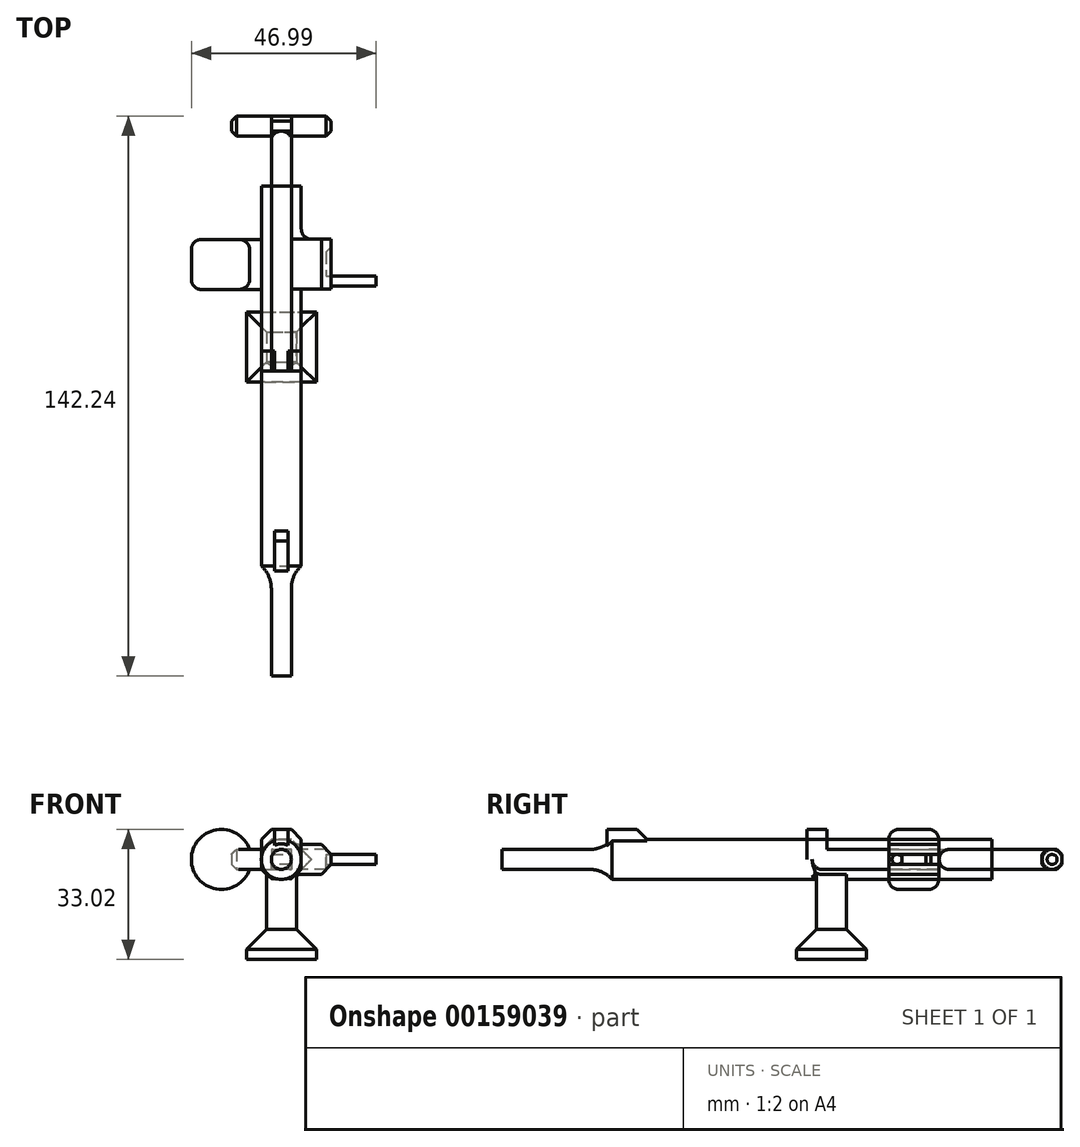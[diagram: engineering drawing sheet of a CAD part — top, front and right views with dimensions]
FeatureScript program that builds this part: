
annotation { "Feature Type Name" : "Feature", "Feature Type Description" : "" }
export const myFeature = defineFeature(function(context is Context, id is Id, definition is map)
    precondition{}
    {
        {
            var Q0;
            Q0=qCreatedBy(makeId("Top.planeOp"),FACE);
            var sketch = newSketch(context, id + "F0", { "sketchPlane" : qUnion([Q0])});
            skLineSegment(sketch, "E0.bottom", {"start": v(5.08, 6.35) * mm, "end": v(-5.08, 6.35) * mm});
            skLineSegment(sketch, "E0.top", {"start": v(5.08, -6.35) * mm, "end": v(-5.08, -6.35) * mm});
            skLineSegment(sketch, "E0.left", {"start": v(5.08, 6.35) * mm, "end": v(5.08, -6.35) * mm});
            skLineSegment(sketch, "E0.right", {"start": v(-5.08, 6.35) * mm, "end": v(-5.08, -6.35) * mm});
            skPoint(sketch, "E0.middle", {"position": v(0, 0) * mm});
            skSolve(sketch);
        }
        {
            var Q0;
            Q0=makeQuery(id+"F0.imprint","IMPRINT",FACE,{"disambiguationData":[TD([[makeQuery(id+"F0.imprint","IMPRINT",EDGE,{"derivedFrom":sQuery(id+"F0.wireOp",EDGE,"E0.bottom")}),1.0]])]});
            extrude(context, id + "F1", {"entities" : qUnion([Q0]), "endBound" : BoundingType.SYMMETRIC, "depth" : 10.16 * mm});
        }
        {
            var Q0;
            Q0=makeQuery(id+"F1.opExtrude","SWEPT_FACE",FACE,{"disambiguationData":[OSD([sQuery(id+"F0.wireOp",EDGE,"E0.top")])]});
            var sketch = newSketch(context, id + "F2", { "sketchPlane" : qUnion([Q0])});
            skCircle(sketch, "E1", {"center": v(0, 0) * mm, "radius": 5.08 * mm});
            skSolve(sketch);
        }
        {
            var Q0;
            {var subQ0=sQuery(id+"F2.wireOp",EDGE,"E1");var subQ1=sQuery(id+"F0.wireOp",EDGE,"E0.top");var subQ2=makeQuery(id+"F2.imprint","INTERSECT",VERTEX,{"derivedFrom":[makeQuery(id+"F1.opExtrude","CAP_EDGE",EDGE,{"disambiguationData":[OSD([subQ1])],"isStart":false}),subQ0]});Q0=makeQuery(id+"F2.imprint","IMPRINT",FACE,{"disambiguationData":[TD([[makeQuery(id+"F2.imprint","IMPRINT",EDGE,{"disambiguationData":[TD([[subQ2,1.0]])],"derivedFrom":subQ0}),1.0]])]});}
            extrude(context, id + "F3", {"entities" : qUnion([Q0]), "operationType" : NewBodyOperationType.ADD, "depth" : 50.8 * mm});
        }
        {
            var Q0;
            Q0=makeQuery(id+"F1.opExtrude","SWEPT_FACE",FACE,{"disambiguationData":[OSD([sQuery(id+"F0.wireOp",EDGE,"E0.bottom")])]});
            extrude(context, id + "F4", {"entities" : qUnion([Q0]), "operationType" : NewBodyOperationType.ADD, "depth" : 25.4 * mm});
        }
        {
            var Q0;
            {var subQ0=sQuery(id+"F0.wireOp",EDGE,"E0.left");var subQ1=sQuery(id+"F0.wireOp",EDGE,"E0.top");Q0=makeQuery(id+"F3.boolean.opBoolean","SPLIT",EDGE,{"disambiguationData":[TD([makeQuery(id+"F1.opExtrude","SWEPT_FACE",FACE,{"disambiguationData":[OSD([subQ0])]})])],"derivedFrom":makeQuery(id+"F1.opExtrude","CAP_EDGE",EDGE,{"disambiguationData":[OSD([subQ1])],"isStart":false})});}
            var Q1;
            {var subQ0=sQuery(id+"F0.wireOp",EDGE,"E0.right");var subQ1=sQuery(id+"F0.wireOp",EDGE,"E0.top");Q1=makeQuery(id+"F3.boolean.opBoolean","SPLIT",EDGE,{"disambiguationData":[TD([makeQuery(id+"F1.opExtrude","SWEPT_FACE",FACE,{"disambiguationData":[OSD([subQ0])]})])],"derivedFrom":makeQuery(id+"F1.opExtrude","CAP_EDGE",EDGE,{"disambiguationData":[OSD([subQ1])],"isStart":true})});}
            fillet(context, id + "F5", {"entities" : qUnion([Q0, Q1]), "radius" : 5.08 * mm, "tangentPropagation" : true, "allowEdgeOverflow" : false});
        }
        {
            var Q0;
            {var subQ0=sQuery(id+"F0.wireOp",EDGE,"E0.right");var subQ1=sQuery(id+"F0.wireOp",EDGE,"E0.bottom");Q0=makeQuery(id+"F4.boolean.opBoolean","MERGE",EDGE,{"derivedFrom":[makeQuery(id+"F1.opExtrude","CAP_EDGE",EDGE,{"disambiguationData":[OSD([subQ0])],"isStart":false}),makeQuery(id+"F4.opExtrude","SWEPT_EDGE",EDGE,{"disambiguationData":[OSD([subQ1,subQ0]),TDD([makeQuery(id+"F1.opExtrude","CAP_VERTEX",VERTEX,{"disambiguationData":[OSD([subQ1,subQ0])],"isStart":false})])]})]});}
            var Q1;
            {var subQ0=sQuery(id+"F0.wireOp",EDGE,"E0.right");var subQ1=sQuery(id+"F0.wireOp",EDGE,"E0.bottom");Q1=makeQuery(id+"F4.boolean.opBoolean","MERGE",EDGE,{"derivedFrom":[makeQuery(id+"F1.opExtrude","CAP_EDGE",EDGE,{"disambiguationData":[OSD([subQ0])],"isStart":true}),makeQuery(id+"F4.opExtrude","SWEPT_EDGE",EDGE,{"disambiguationData":[OSD([subQ1,subQ0]),TDD([makeQuery(id+"F1.opExtrude","CAP_VERTEX",VERTEX,{"disambiguationData":[OSD([subQ1,subQ0])],"isStart":true})])]})]});}
            var Q2;
            {var subQ0=sQuery(id+"F0.wireOp",EDGE,"E0.left");var subQ1=sQuery(id+"F0.wireOp",EDGE,"E0.bottom");Q2=makeQuery(id+"F4.boolean.opBoolean","MERGE",EDGE,{"derivedFrom":[makeQuery(id+"F1.opExtrude","CAP_EDGE",EDGE,{"disambiguationData":[OSD([subQ0])],"isStart":false}),makeQuery(id+"F4.opExtrude","SWEPT_EDGE",EDGE,{"disambiguationData":[OSD([subQ1,subQ0]),TDD([makeQuery(id+"F1.opExtrude","CAP_VERTEX",VERTEX,{"disambiguationData":[OSD([subQ1,subQ0])],"isStart":false})])]})]});}
            var Q3;
            {var subQ0=sQuery(id+"F0.wireOp",EDGE,"E0.left");var subQ1=sQuery(id+"F0.wireOp",EDGE,"E0.bottom");Q3=makeQuery(id+"F4.boolean.opBoolean","MERGE",EDGE,{"derivedFrom":[makeQuery(id+"F1.opExtrude","CAP_EDGE",EDGE,{"disambiguationData":[OSD([subQ0])],"isStart":true}),makeQuery(id+"F4.opExtrude","SWEPT_EDGE",EDGE,{"disambiguationData":[OSD([subQ1,subQ0]),TDD([makeQuery(id+"F1.opExtrude","CAP_VERTEX",VERTEX,{"disambiguationData":[OSD([subQ1,subQ0])],"isStart":true})])]})]});}
            var Q4;
            Q4=makeQuery(id+"F3.opExtrude","CAP_EDGE",EDGE,{"disambiguationData":[OSD([sQuery(id+"F2.wireOp",EDGE,"E1")])],"isStart":false});
            chamfer(context, id + "F6", {"entities" : qUnion([Q0, Q1, Q2, Q3, Q4]), "width" : 2.54 * mm, "tangentPropagation" : true});
        }
        {
            var Q0;
            {var subQ0=sQuery(id+"F0.wireOp",EDGE,"E0.bottom");Q0=makeQuery(id+"F4.boolean.opBoolean","MERGE",FACE,{"derivedFrom":[makeQuery(id+"F1.opExtrude","CAP_FACE",FACE,{"disambiguationData":[OSD([subQ0,sQuery(id+"F0.wireOp",EDGE,"E0.top"),sQuery(id+"F0.wireOp",EDGE,"E0.left"),sQuery(id+"F0.wireOp",EDGE,"E0.right")])],"isStart":true}),makeQuery(id+"F4.opExtrude","SWEPT_FACE",FACE,{"disambiguationData":[OSD([subQ0]),TDD([makeQuery(id+"F1.opExtrude","CAP_EDGE",EDGE,{"disambiguationData":[OSD([subQ0])],"isStart":true})])]})]});}
            var sketch = newSketch(context, id + "F7", { "sketchPlane" : qUnion([Q0])});
            skPoint(sketch, "E2.middle", {"position": v(0, 0) * mm});
            skLineSegment(sketch, "E3.bottom", {"start": v(-3.8, -4.85) * mm, "end": v(3.81, -4.85) * mm});
            skLineSegment(sketch, "E3.top", {"start": v(-3.81, 2.77) * mm, "end": v(3.8, 2.77) * mm});
            skLineSegment(sketch, "E3.left", {"start": v(-3.8, -4.85) * mm, "end": v(-3.81, 2.77) * mm});
            skLineSegment(sketch, "E3.right", {"start": v(3.81, -4.85) * mm, "end": v(3.8, 2.77) * mm});
            skPoint(sketch, "E3.middle", {"position": v(0, -1.04) * mm});
            skSolve(sketch);
        }
        {
            var Q0;
            Q0 = qSketchRegion(id + "F7", true);
            extrude(context, id + "F8", {"entities" : qUnion([Q0]), "operationType" : NewBodyOperationType.ADD, "endBound" : BoundingType.SYMMETRIC, "depth" : 15.24 * mm});
        }
        {
            var Q0;
            Q0=makeQuery(id+"F8.opExtrude","CAP_FACE",FACE,{"disambiguationData":[OSD([sQuery(id+"F7.wireOp",EDGE,"E3.bottom"),sQuery(id+"F7.wireOp",EDGE,"E3.top"),sQuery(id+"F7.wireOp",EDGE,"E3.left"),sQuery(id+"F7.wireOp",EDGE,"E3.right")])],"isStart":false});
            extrude(context, id + "F9", {"entities" : qUnion([Q0]), "operationType" : NewBodyOperationType.ADD, "depth" : 5.08 * mm});
        }
        {
            var Q0;
            Q0=makeQuery(id+"F9.opExtrude","CAP_FACE",FACE,{"disambiguationData":[OSD([sQuery(id+"F7.wireOp",EDGE,"E3.bottom"),sQuery(id+"F7.wireOp",EDGE,"E3.top"),sQuery(id+"F7.wireOp",EDGE,"E3.left"),sQuery(id+"F7.wireOp",EDGE,"E3.right")])],"isStart":false});
            var sketch = newSketch(context, id + "F10", { "sketchPlane" : qUnion([Q0])});
            skLineSegment(sketch, "E4.bottom", {"start": v(-8.9, -9.93) * mm, "end": v(8.9, -9.93) * mm});
            skLineSegment(sketch, "E4.top", {"start": v(-8.9, 7.85) * mm, "end": v(8.89, 7.85) * mm});
            skLineSegment(sketch, "E4.left", {"start": v(-8.9, -9.93) * mm, "end": v(-8.9, 7.85) * mm});
            skLineSegment(sketch, "E4.right", {"start": v(8.9, -9.93) * mm, "end": v(8.89, 7.85) * mm});
            skPoint(sketch, "E4.middle", {"position": v(0, -1.04) * mm});
            skPoint(sketch, "E4.middle.positionSnap0", {"position": v(3.8, -1.04) * mm});
            skPoint(sketch, "E4.centerSnap0", {"position": v(3.8, -1.04) * mm});
            skSolve(sketch);
        }
        {
            var Q0;
            Q0 = qSketchRegion(id + "F10", true);
            extrude(context, id + "F11", {"entities" : qUnion([Q0]), "operationType" : NewBodyOperationType.ADD, "depth" : 7.62 * mm});
        }
        {
            var Q0;
            {var subQ0=sQuery(id+"F0.wireOp",EDGE,"E0.right");Q0=makeQuery(id+"F4.boolean.opBoolean","MERGE",FACE,{"derivedFrom":[makeQuery(id+"F1.opExtrude","SWEPT_FACE",FACE,{"disambiguationData":[OSD([subQ0])]}),makeQuery(id+"F4.opExtrude","SWEPT_FACE",FACE,{"disambiguationData":[OSD([sQuery(id+"F0.wireOp",EDGE,"E0.bottom"),subQ0])]})]});}
            var sketch = newSketch(context, id + "F12", { "sketchPlane" : qUnion([Q0])});
            skLineSegment(sketch, "E5.bottom", {"start": v(-28.34, 2.54) * mm, "end": v(-15.64, 2.54) * mm});
            skLineSegment(sketch, "E5.top", {"start": v(-28.34, -2.54) * mm, "end": v(-15.64, -2.54) * mm});
            skLineSegment(sketch, "E5.left", {"start": v(-28.34, 2.54) * mm, "end": v(-28.34, -2.54) * mm});
            skLineSegment(sketch, "E5.right", {"start": v(-15.64, 2.54) * mm, "end": v(-15.64, -2.54) * mm});
            skPoint(sketch, "E5.middle", {"position": v(-22, 0) * mm});
            skSolve(sketch);
        }
        {
            var Q0;
            Q0=makeQuery(id+"F12.imprint","IMPRINT",FACE,{"disambiguationData":[TD([[makeQuery(id+"F12.imprint","IMPRINT",EDGE,{"derivedFrom":sQuery(id+"F12.wireOp",EDGE,"E5.bottom")}),1.0]])]});
            extrude(context, id + "F13", {"entities" : qUnion([Q0]), "operationType" : NewBodyOperationType.ADD, "depth" : 5.08 * mm});
        }
        {
            var Q0;
            Q0=makeQuery(id+"F13.opExtrude","SWEPT_FACE",FACE,{"disambiguationData":[OSD([sQuery(id+"F12.wireOp",EDGE,"E5.left")])]});
            var sketch = newSketch(context, id + "F14", { "sketchPlane" : qUnion([Q0])});
            skCircle(sketch, "E6", {"center": v(15.24, 0) * mm, "radius": 7.62 * mm});
            skPoint(sketch, "E6.centerSnap0", {"position": v(10.16, 0) * mm});
            skSolve(sketch);
        }
        {
            var Q0;
            Q0 = qSketchRegion(id + "F14", true);
            extrude(context, id + "F15", {"entities" : qUnion([Q0]), "operationType" : NewBodyOperationType.ADD, "oppositeDirection" : true, "depth" : 12.7 * mm});
        }
        {
            var Q0;
            Q0=makeQuery(id+"F4.opExtrude","CAP_FACE",FACE,{"disambiguationData":[OSD([sQuery(id+"F0.wireOp",EDGE,"E0.bottom")])],"isStart":false});
            extrude(context, id + "F16", {"entities" : qUnion([Q0]), "operationType" : NewBodyOperationType.ADD, "depth" : 10.16 * mm});
        }
        {
            var Q0;
            Q0=makeQuery(id+"F15.opExtrude","CAP_EDGE",EDGE,{"disambiguationData":[OSD([sQuery(id+"F14.wireOp",EDGE,"E6")])],"isStart":true});
            var Q1;
            Q1=makeQuery(id+"F15.opExtrude","CAP_EDGE",EDGE,{"disambiguationData":[OSD([sQuery(id+"F14.wireOp",EDGE,"E6")])],"isStart":false});
            fillet(context, id + "F17", {"entities" : qUnion([Q0, Q1]), "radius" : 2.54 * mm, "tangentPropagation" : true, "allowEdgeOverflow" : false});
        }
        {
            var Q0;
            Q0=makeQuery(id+"F11.opExtrude","CAP_EDGE",EDGE,{"disambiguationData":[OSD([sQuery(id+"F10.wireOp",EDGE,"E4.right")])],"isStart":true});
            var Q1;
            Q1=makeQuery(id+"F11.opExtrude","CAP_EDGE",EDGE,{"disambiguationData":[OSD([sQuery(id+"F10.wireOp",EDGE,"E4.bottom")])],"isStart":true});
            var Q2;
            Q2=makeQuery(id+"F11.opExtrude","CAP_EDGE",EDGE,{"disambiguationData":[OSD([sQuery(id+"F10.wireOp",EDGE,"E4.top")])],"isStart":true});
            var Q3;
            Q3=makeQuery(id+"F11.opExtrude","CAP_EDGE",EDGE,{"disambiguationData":[OSD([sQuery(id+"F10.wireOp",EDGE,"E4.left")])],"isStart":true});
            chamfer(context, id + "F18", {"entities" : qUnion([Q0, Q1, Q2, Q3]), "width" : 5.08 * mm, "tangentPropagation" : true});
        }
        {
            var Q0;
            Q0=makeQuery(id+"F16.opExtrude","CAP_FACE",FACE,{"disambiguationData":[OSD([sQuery(id+"F0.wireOp",EDGE,"E0.bottom")])],"isStart":false});
            var sketch = newSketch(context, id + "F19", { "sketchPlane" : qUnion([Q0])});
            skCircle(sketch, "E7", {"center": v(0, 0) * mm, "radius": 2.54 * mm});
            skSolve(sketch);
        }
        {
            var Q0;
            Q0=makeQuery(id+"F19.imprint","IMPRINT",FACE,{"disambiguationData":[TD([[makeQuery(id+"F19.imprint","IMPRINT",EDGE,{"derivedFrom":sQuery(id+"F19.wireOp",EDGE,"E7")}),1.0]])]});
            extrude(context, id + "F20", {"entities" : qUnion([Q0]), "operationType" : NewBodyOperationType.ADD, "depth" : 12.7 * mm});
        }
        {
            var Q0;
            Q0=makeQuery(id+"F20.opExtrude","CAP_FACE",FACE,{"disambiguationData":[OSD([sQuery(id+"F19.wireOp",EDGE,"E7")])],"isStart":false});
            var sketch = newSketch(context, id + "F21", { "sketchPlane" : qUnion([Q0])});
            skLineSegment(sketch, "E8.bottom", {"start": v(2.54, 2.54) * mm, "end": v(-2.54, 2.54) * mm});
            skLineSegment(sketch, "E8.top", {"start": v(2.54, -2.54) * mm, "end": v(-2.54, -2.54) * mm});
            skLineSegment(sketch, "E8.left", {"start": v(2.54, 2.54) * mm, "end": v(2.54, -2.54) * mm});
            skLineSegment(sketch, "E8.right", {"start": v(-2.54, 2.54) * mm, "end": v(-2.54, -2.54) * mm});
            skPoint(sketch, "E8.middle", {"position": v(0, 0) * mm});
            skSolve(sketch);
        }
        {
            var Q0;
            Q0 = qSketchRegion(id + "F21", true);
            extrude(context, id + "F22", {"entities" : qUnion([Q0]), "operationType" : NewBodyOperationType.ADD, "depth" : 5.08 * mm});
        }
        {
            var Q0;
            Q0=makeQuery(id+"F22.opExtrude","SWEPT_FACE",FACE,{"disambiguationData":[OSD([sQuery(id+"F21.wireOp",EDGE,"E8.right")])]});
            var sketch = newSketch(context, id + "F23", { "sketchPlane" : qUnion([Q0])});
            skCircle(sketch, "E9", {"center": v(57.15, 0) * mm, "radius": 2.54 * mm});
            skSolve(sketch);
        }
        {
            var Q0;
            {var subQ0=sQuery(id+"F23.wireOp",EDGE,"E9");var subQ1=sQuery(id+"F21.wireOp",EDGE,"E8.right");var subQ4=makeQuery(id+"F23.imprint","INTERSECT",VERTEX,{"derivedFrom":[makeQuery(id+"F22.opExtrude","CAP_EDGE",EDGE,{"disambiguationData":[OSD([subQ1])],"isStart":false}),subQ0]});Q0=makeQuery(id+"F23.imprint","IMPRINT",FACE,{"disambiguationData":[TD([[makeQuery(id+"F23.imprint","IMPRINT",EDGE,{"disambiguationData":[TD([[subQ4,-1.0]])],"derivedFrom":subQ0}),1.0]])]});}
            extrude(context, id + "F24", {"entities" : qUnion([Q0]), "operationType" : NewBodyOperationType.ADD, "depth" : 10.16 * mm});
        }
        {
            var Q0;
            Q0=makeQuery(id+"F22.opExtrude","SWEPT_FACE",FACE,{"disambiguationData":[OSD([sQuery(id+"F21.wireOp",EDGE,"E8.left")])]});
            var sketch = newSketch(context, id + "F25", { "sketchPlane" : qUnion([Q0])});
            skCircle(sketch, "E10", {"center": v(-57.15, 0) * mm, "radius": 2.54 * mm});
            skSolve(sketch);
        }
        {
            var Q0;
            Q0 = qSketchRegion(id + "F25", true);
            extrude(context, id + "F26", {"entities" : qUnion([Q0]), "operationType" : NewBodyOperationType.ADD, "depth" : 10.16 * mm});
        }
        {
            var Q0;
            Q0=makeQuery(id+"F22.opExtrude","CAP_EDGE",EDGE,{"disambiguationData":[OSD([sQuery(id+"F21.wireOp",EDGE,"E8.bottom")])],"isStart":false});
            var Q1;
            Q1=makeQuery(id+"F22.opExtrude","CAP_EDGE",EDGE,{"disambiguationData":[OSD([sQuery(id+"F21.wireOp",EDGE,"E8.top")])],"isStart":false});
            var Q2;
            {var subQ0=sQuery(id+"F21.wireOp",EDGE,"E8.bottom");var subQ1=sQuery(id+"F21.wireOp",EDGE,"E8.left");Q2=makeQuery(id+"F22.boolean.opBoolean","SPLIT",EDGE,{"disambiguationData":[TD([makeQuery(id+"F22.opExtrude","SWEPT_FACE",FACE,{"disambiguationData":[OSD([subQ1])]})])],"derivedFrom":makeQuery(id+"F22.opExtrude","CAP_EDGE",EDGE,{"disambiguationData":[OSD([subQ0])],"isStart":true})});}
            var Q3;
            {var subQ0=sQuery(id+"F21.wireOp",EDGE,"E8.left");var subQ1=sQuery(id+"F21.wireOp",EDGE,"E8.top");Q3=makeQuery(id+"F22.boolean.opBoolean","SPLIT",EDGE,{"disambiguationData":[TD([makeQuery(id+"F22.opExtrude","SWEPT_FACE",FACE,{"disambiguationData":[OSD([subQ0])]})])],"derivedFrom":makeQuery(id+"F22.opExtrude","CAP_EDGE",EDGE,{"disambiguationData":[OSD([subQ1])],"isStart":true})});}
            var Q4;
            Q4=makeQuery(id+"F26.opExtrude","CAP_EDGE",EDGE,{"disambiguationData":[OSD([sQuery(id+"F25.wireOp",EDGE,"E10")])],"isStart":false});
            var Q5;
            Q5=makeQuery(id+"F24.opExtrude","CAP_EDGE",EDGE,{"disambiguationData":[OSD([sQuery(id+"F23.wireOp",EDGE,"E9")])],"isStart":false});
            chamfer(context, id + "F27", {"entities" : qUnion([Q0, Q1, Q2, Q3, Q4, Q5]), "width" : 1.27 * mm, "tangentPropagation" : true});
        }
        {
            var Q0;
            Q0=qCreatedBy(makeId("Top.planeOp"),FACE);
            var sketch = newSketch(context, id + "F28", { "sketchPlane" : qUnion([Q0])});
            skLineSegment(sketch, "E11.bottom", {"start": v(-5.08, -5.08) * mm, "end": v(5.08, -5.08) * mm});
            skLineSegment(sketch, "E11.top", {"start": v(-5.08, 0) * mm, "end": v(5.08, 0) * mm});
            skLineSegment(sketch, "E11.left", {"start": v(-5.08, -5.08) * mm, "end": v(-5.08, 0) * mm});
            skLineSegment(sketch, "E11.right", {"start": v(5.08, -5.08) * mm, "end": v(5.08, 0) * mm});
            skPoint(sketch, "E11.middle", {"position": v(0, -2.54) * mm});
            skLineSegment(sketch, "E12.bottom", {"start": v(-1.78, -45.72) * mm, "end": v(1.78, -45.72) * mm});
            skLineSegment(sketch, "E12.top", {"start": v(-1.78, -55.88) * mm, "end": v(1.78, -55.88) * mm});
            skLineSegment(sketch, "E12.left", {"start": v(-1.78, -45.72) * mm, "end": v(-1.78, -55.88) * mm});
            skLineSegment(sketch, "E12.right", {"start": v(1.78, -45.72) * mm, "end": v(1.78, -55.88) * mm});
            skPoint(sketch, "E12.middle", {"position": v(0, -50.8) * mm});
            skLineSegment(sketch, "E13", {"start": v(1.78, 0) * mm, "end": v(1.78, -5.08) * mm});
            skLineSegment(sketch, "E14", {"start": v(-1.78, 0) * mm, "end": v(-1.78, -5.08) * mm});
            skSolve(sketch);
        }
        {
            var Q0;
            Q0 = qSketchRegion(id + "F28", true);
            extrude(context, id + "F29", {"entities" : qUnion([Q0]), "operationType" : NewBodyOperationType.ADD, "depth" : 7.62 * mm});
        }
        {
            var Q0;
            Q0=makeQuery(id+"F29.opExtrude","CAP_FACE",FACE,{"disambiguationData":[OSD([sQuery(id+"F28.wireOp",EDGE,"E11.bottom"),sQuery(id+"F28.wireOp",EDGE,"E11.top"),sQuery(id+"F28.wireOp",EDGE,"E11.left"),sQuery(id+"F28.wireOp",EDGE,"E11.right")])],"isStart":false});
            var sketch = newSketch(context, id + "F30", { "sketchPlane" : qUnion([Q0])});
            skLineSegment(sketch, "E15.bottom", {"start": v(-1.78, 0) * mm, "end": v(1.78, 0) * mm});
            skLineSegment(sketch, "E15.top", {"start": v(-1.78, -5.08) * mm, "end": v(1.78, -5.08) * mm});
            skLineSegment(sketch, "E15.left", {"start": v(-1.78, 0) * mm, "end": v(-1.78, -5.08) * mm});
            skLineSegment(sketch, "E15.right", {"start": v(1.78, 0) * mm, "end": v(1.78, -5.08) * mm});
            skSolve(sketch);
        }
        {
            var Q0;
            Q0=makeQuery(id+"F30.imprint","IMPRINT",FACE,{"disambiguationData":[TD([[makeQuery(id+"F30.imprint","IMPRINT",EDGE,{"derivedFrom":sQuery(id+"F30.wireOp",EDGE,"E15.left")}),1.0]])]});
            extrude(context, id + "F31", {"entities" : qUnion([Q0]), "operationType" : NewBodyOperationType.REMOVE, "oppositeDirection" : true, "depth" : 2.54 * mm});
        }
        {
            var Q0;
            Q0=makeQuery(id+"F29.opExtrude","CAP_EDGE",EDGE,{"disambiguationData":[OSD([sQuery(id+"F28.wireOp",EDGE,"E11.right")])],"isStart":false});
            var Q1;
            Q1=makeQuery(id+"F29.opExtrude","CAP_EDGE",EDGE,{"disambiguationData":[OSD([sQuery(id+"F28.wireOp",EDGE,"E11.left")])],"isStart":false});
            var Q2;
            Q2=makeQuery(id+"F29.opExtrude","CAP_EDGE",EDGE,{"disambiguationData":[OSD([sQuery(id+"F28.wireOp",EDGE,"E12.bottom")])],"isStart":false});
            chamfer(context, id + "F32", {"entities" : qUnion([Q0, Q1, Q2]), "width" : 2.54 * mm, "tangentPropagation" : true});
        }
        {
            var Q0;
            {var subQ0=sQuery(id+"F0.wireOp",EDGE,"E0.left");var subQ1=sQuery(id+"F0.wireOp",EDGE,"E0.bottom");Q0=makeQuery(id+"F29.boolean.opBoolean","MERGE",FACE,{"derivedFrom":[makeQuery(id+"F16.boolean.opBoolean","MERGE",FACE,{"derivedFrom":[makeQuery(id+"F4.boolean.opBoolean","MERGE",FACE,{"derivedFrom":[makeQuery(id+"F1.opExtrude","SWEPT_FACE",FACE,{"disambiguationData":[OSD([subQ0])]}),makeQuery(id+"F4.opExtrude","SWEPT_FACE",FACE,{"disambiguationData":[OSD([subQ1,subQ0])]})]}),makeQuery(id+"F16.opExtrude","SWEPT_FACE",FACE,{"disambiguationData":[OSD([subQ1,subQ0]),TDD([makeQuery(id+"F4.opExtrude","CAP_EDGE",EDGE,{"disambiguationData":[OSD([subQ1,subQ0])],"isStart":false})])]})]}),makeQuery(id+"F29.opExtrude","SWEPT_FACE",FACE,{"disambiguationData":[OSD([sQuery(id+"F28.wireOp",EDGE,"E11.right")])]})]});}
            var sketch = newSketch(context, id + "F33", { "sketchPlane" : qUnion([Q0])});
            skLineSegment(sketch, "E16.bottom", {"start": v(15.75, 3.81) * mm, "end": v(28.45, 3.81) * mm});
            skLineSegment(sketch, "E16.top", {"start": v(15.75, -3.8) * mm, "end": v(28.45, -3.8) * mm});
            skLineSegment(sketch, "E16.left", {"start": v(15.75, 3.81) * mm, "end": v(15.75, -3.8) * mm});
            skLineSegment(sketch, "E16.right", {"start": v(28.45, 3.81) * mm, "end": v(28.45, -3.8) * mm});
            skSolve(sketch);
        }
        {
            var Q0;
            Q0 = qSketchRegion(id + "F33", true);
            extrude(context, id + "F34", {"entities" : qUnion([Q0]), "operationType" : NewBodyOperationType.ADD, "depth" : 7.62 * mm});
        }
        {
            var Q0;
            Q0=makeQuery(id+"F34.opExtrude","CAP_EDGE",EDGE,{"disambiguationData":[OSD([sQuery(id+"F33.wireOp",EDGE,"E16.bottom")])],"isStart":false});
            var Q1;
            Q1=makeQuery(id+"F34.opExtrude","CAP_EDGE",EDGE,{"disambiguationData":[OSD([sQuery(id+"F33.wireOp",EDGE,"E16.top")])],"isStart":false});
            chamfer(context, id + "F35", {"entities" : qUnion([Q0, Q1]), "width" : 2.54 * mm, "tangentPropagation" : true});
        }
        {
            var Q0;
            Q0=makeQuery(id+"F3.opExtrude","CAP_FACE",FACE,{"disambiguationData":[OSD([sQuery(id+"F2.wireOp",EDGE,"E1")])],"isStart":false});
            extrude(context, id + "F36", {"entities" : qUnion([Q0]), "operationType" : NewBodyOperationType.ADD, "depth" : 25.4 * mm});
        }
        {
            var Q0;
            {var subQ0=sQuery(id+"F2.wireOp",EDGE,"E1");Q0=makeQuery(id+"F36.boolean.opBoolean","MERGE",EDGE,{"derivedFrom":[makeQuery(id+"F6.opChamfer","BLEND_EDGE",EDGE,{"blendedFrom":[makeQuery(id+"F3.opExtrude","CAP_EDGE",EDGE,{"disambiguationData":[OSD([subQ0])],"isStart":false}),makeQuery(id+"F3.opExtrude","CAP_FACE",FACE,{"disambiguationData":[OSD([subQ0])],"isStart":false})],"blendedInto":[makeQuery(id+"F3.opExtrude","CAP_FACE",FACE,{"disambiguationData":[OSD([subQ0])],"isStart":false})]}),makeQuery(id+"F36.opExtrude","CAP_EDGE",EDGE,{"disambiguationData":[OSD([subQ0])],"isStart":true})]});}
            fillet(context, id + "F37", {"entities" : qUnion([Q0]), "radius" : 7.62 * mm, "tangentPropagation" : true, "allowEdgeOverflow" : false});
        }
        {
            var Q0;
            Q0=makeQuery(id+"F34.opExtrude","CAP_FACE",FACE,{"disambiguationData":[OSD([sQuery(id+"F33.wireOp",EDGE,"E16.bottom"),sQuery(id+"F33.wireOp",EDGE,"E16.top"),sQuery(id+"F33.wireOp",EDGE,"E16.left"),sQuery(id+"F33.wireOp",EDGE,"E16.right")])],"isStart":false});
            var sketch = newSketch(context, id + "F38", { "sketchPlane" : qUnion([Q0])});
            skLineSegment(sketch, "E17.bottom", {"start": v(19.05, 1.27) * mm, "end": v(25.15, 1.27) * mm});
            skLineSegment(sketch, "E17.top", {"start": v(19.05, -1.27) * mm, "end": v(25.15, -1.27) * mm});
            skLineSegment(sketch, "E17.left", {"start": v(19.05, 1.27) * mm, "end": v(19.05, -1.27) * mm});
            skLineSegment(sketch, "E17.right", {"start": v(25.15, 1.27) * mm, "end": v(25.15, -1.27) * mm});
            skSolve(sketch);
        }
        {
            var Q0;
            Q0=makeQuery(id+"F38.imprint","IMPRINT",FACE,{"disambiguationData":[TD([[makeQuery(id+"F38.imprint","IMPRINT",EDGE,{"derivedFrom":sQuery(id+"F38.wireOp",EDGE,"E17.bottom")}),1.0]])]});
            extrude(context, id + "F39", {"entities" : qUnion([Q0]), "operationType" : NewBodyOperationType.REMOVE, "oppositeDirection" : true, "depth" : 1.27 * mm});
        }
        {
            var Q0;
            Q0=makeQuery(id+"F39.boolean.opBoolean","COPY",EDGE,{"derivedFrom":makeQuery(id+"F39.opExtrude","CAP_EDGE",EDGE,{"disambiguationData":[OSD([sQuery(id+"F38.wireOp",EDGE,"E17.right")])],"isStart":true})});
            var Q1;
            Q1=makeQuery(id+"F39.boolean.opBoolean","COPY",EDGE,{"derivedFrom":makeQuery(id+"F39.opExtrude","CAP_EDGE",EDGE,{"disambiguationData":[OSD([sQuery(id+"F38.wireOp",EDGE,"E17.left")])],"isStart":true})});
            chamfer(context, id + "F40", {"entities" : qUnion([Q0, Q1]), "width" : 1.27 * mm, "tangentPropagation" : true});
        }
        {
            var Q0;
            Q0=makeQuery(id+"F39.boolean.opBoolean","COPY",FACE,{"derivedFrom":makeQuery(id+"F39.opExtrude","CAP_FACE",FACE,{"disambiguationData":[OSD([sQuery(id+"F38.wireOp",EDGE,"E17.bottom"),sQuery(id+"F38.wireOp",EDGE,"E17.top"),sQuery(id+"F38.wireOp",EDGE,"E17.left"),sQuery(id+"F38.wireOp",EDGE,"E17.right")])],"isStart":false})});
            var sketch = newSketch(context, id + "F41", { "sketchPlane" : qUnion([Q0])});
            skCircle(sketch, "E18", {"center": v(17.78, 0) * mm, "radius": 1.27 * mm});
            skSolve(sketch);
        }
        {
            var Q0;
            Q0 = qSketchRegion(id + "F41", true);
            extrude(context, id + "F42", {"entities" : qUnion([Q0]), "operationType" : NewBodyOperationType.ADD, "depth" : 12.7 * mm});
        }
        {
            var Q0;
            {var subQ2=sQuery(id+"F33.wireOp",EDGE,"E16.left");var subQ4=sQuery(id+"F33.wireOp",EDGE,"E16.bottom");var subQ5=sQuery(id+"F33.wireOp",EDGE,"E16.right");Q0=makeQuery(id+"F34.boolean.opBoolean","SPLIT",FACE,{"disambiguationData":[TD([makeQuery(id+"F34.opExtrude","SWEPT_FACE",FACE,{"disambiguationData":[OSD([subQ4])]})])],"derivedFrom":makeQuery(id+"F34.opExtrude","CAP_FACE",FACE,{"disambiguationData":[OSD([subQ4,sQuery(id+"F33.wireOp",EDGE,"E16.top"),subQ2,subQ5])],"isStart":true})});}
            var Q1;
            {var subQ2=sQuery(id+"F33.wireOp",EDGE,"E16.left");var subQ4=sQuery(id+"F33.wireOp",EDGE,"E16.top");var subQ5=sQuery(id+"F33.wireOp",EDGE,"E16.right");Q1=makeQuery(id+"F34.boolean.opBoolean","SPLIT",FACE,{"disambiguationData":[TD([makeQuery(id+"F34.opExtrude","SWEPT_FACE",FACE,{"disambiguationData":[OSD([subQ4])]})])],"derivedFrom":makeQuery(id+"F34.opExtrude","CAP_FACE",FACE,{"disambiguationData":[OSD([sQuery(id+"F33.wireOp",EDGE,"E16.bottom"),subQ4,subQ2,subQ5])],"isStart":true})});}
            extrude(context, id + "F43", {"entities" : qUnion([Q0, Q1]), "operationType" : NewBodyOperationType.ADD, "depth" : 7.62 * mm});
        }
        {
            var Q0;
            {var subQ0=sQuery(id+"F0.wireOp",EDGE,"E0.bottom");var subQ1=sQuery(id+"F0.wireOp",EDGE,"E0.left");var subQ2=makeQuery(id+"F4.boolean.opBoolean","MERGE",EDGE,{"derivedFrom":[makeQuery(id+"F1.opExtrude","CAP_EDGE",EDGE,{"disambiguationData":[OSD([subQ1])],"isStart":false}),makeQuery(id+"F4.opExtrude","SWEPT_EDGE",EDGE,{"disambiguationData":[OSD([subQ0,subQ1]),TDD([makeQuery(id+"F1.opExtrude","CAP_VERTEX",VERTEX,{"disambiguationData":[OSD([subQ0,subQ1])],"isStart":false})])]})]});Q0=makeQuery(id+"F43.boolean.opBoolean","INTERSECT",EDGE,{"derivedFrom":[makeQuery(id+"F16.boolean.opBoolean","MERGE",FACE,{"derivedFrom":[makeQuery(id+"F6.opChamfer","BLEND_FACE",FACE,{"disambiguationData":[OSD([subQ0,subQ1]),TDD([subQ2])]}),makeQuery(id+"F16.opExtrude","SWEPT_FACE",FACE,{"disambiguationData":[OSD([subQ0,subQ1]),TDD([makeQuery(id+"F6.opChamfer","BLEND_EDGE",EDGE,{"blendedFrom":[subQ2,makeQuery(id+"F4.opExtrude","CAP_FACE",FACE,{"disambiguationData":[OSD([subQ0])],"isStart":false})],"blendedInto":[makeQuery(id+"F4.opExtrude","CAP_FACE",FACE,{"disambiguationData":[OSD([subQ0])],"isStart":false})]})])]})]}),makeQuery(id+"F43.opExtrude","SWEPT_FACE",FACE,{"disambiguationData":[OSD([sQuery(id+"F33.wireOp",EDGE,"E16.bottom")])]})]});}
            var Q1;
            {var subQ0=sQuery(id+"F0.wireOp",EDGE,"E0.left");var subQ1=sQuery(id+"F0.wireOp",EDGE,"E0.bottom");var subQ2=sQuery(id+"F33.wireOp",EDGE,"E16.left");Q1=makeQuery(id+"F34.boolean.opBoolean","SPLIT",EDGE,{"disambiguationData":[topologyDisambiguationEdgeConnected([makeQuery(id+"F1.opExtrude","SWEPT_FACE",FACE,{"disambiguationData":[OSD([subQ0])]}),makeQuery(id+"F4.opExtrude","SWEPT_FACE",FACE,{"disambiguationData":[OSD([subQ1,subQ0])]}),makeQuery(id+"F16.opExtrude","SWEPT_FACE",FACE,{"disambiguationData":[OSD([subQ1,subQ0]),TDD([makeQuery(id+"F4.opExtrude","CAP_EDGE",EDGE,{"disambiguationData":[OSD([subQ1,subQ0])],"isStart":false})])]}),makeQuery(id+"F29.opExtrude","SWEPT_FACE",FACE,{"disambiguationData":[OSD([sQuery(id+"F28.wireOp",EDGE,"E11.right")])]}),makeQuery(id+"F34.opExtrude","SWEPT_FACE",FACE,{"disambiguationData":[OSD([subQ2])]})])],"derivedFrom":makeQuery(id+"F34.opExtrude","CAP_EDGE",EDGE,{"disambiguationData":[OSD([subQ2])],"isStart":true})});}
            var Q2;
            {var subQ0=sQuery(id+"F0.wireOp",EDGE,"E0.left");var subQ1=sQuery(id+"F0.wireOp",EDGE,"E0.bottom");var subQ2=sQuery(id+"F33.wireOp",EDGE,"E16.right");Q2=makeQuery(id+"F34.boolean.opBoolean","SPLIT",EDGE,{"disambiguationData":[topologyDisambiguationEdgeConnected([makeQuery(id+"F1.opExtrude","SWEPT_FACE",FACE,{"disambiguationData":[OSD([subQ0])]}),makeQuery(id+"F4.opExtrude","SWEPT_FACE",FACE,{"disambiguationData":[OSD([subQ1,subQ0])]}),makeQuery(id+"F16.opExtrude","SWEPT_FACE",FACE,{"disambiguationData":[OSD([subQ1,subQ0]),TDD([makeQuery(id+"F4.opExtrude","CAP_EDGE",EDGE,{"disambiguationData":[OSD([subQ1,subQ0])],"isStart":false})])]}),makeQuery(id+"F29.opExtrude","SWEPT_FACE",FACE,{"disambiguationData":[OSD([sQuery(id+"F28.wireOp",EDGE,"E11.right")])]}),makeQuery(id+"F34.opExtrude","SWEPT_FACE",FACE,{"disambiguationData":[OSD([subQ2])]})])],"derivedFrom":makeQuery(id+"F34.opExtrude","CAP_EDGE",EDGE,{"disambiguationData":[OSD([subQ2])],"isStart":true})});}
            var Q3;
            {var subQ0=sQuery(id+"F0.wireOp",EDGE,"E0.bottom");var subQ1=sQuery(id+"F0.wireOp",EDGE,"E0.left");var subQ2=makeQuery(id+"F4.boolean.opBoolean","MERGE",EDGE,{"derivedFrom":[makeQuery(id+"F1.opExtrude","CAP_EDGE",EDGE,{"disambiguationData":[OSD([subQ1])],"isStart":true}),makeQuery(id+"F4.opExtrude","SWEPT_EDGE",EDGE,{"disambiguationData":[OSD([subQ0,subQ1]),TDD([makeQuery(id+"F1.opExtrude","CAP_VERTEX",VERTEX,{"disambiguationData":[OSD([subQ0,subQ1])],"isStart":true})])]})]});Q3=makeQuery(id+"F43.boolean.opBoolean","INTERSECT",EDGE,{"derivedFrom":[makeQuery(id+"F16.boolean.opBoolean","MERGE",FACE,{"derivedFrom":[makeQuery(id+"F6.opChamfer","BLEND_FACE",FACE,{"disambiguationData":[OSD([subQ0,subQ1]),TDD([subQ2])]}),makeQuery(id+"F16.opExtrude","SWEPT_FACE",FACE,{"disambiguationData":[OSD([subQ0,subQ1]),TDD([makeQuery(id+"F6.opChamfer","BLEND_EDGE",EDGE,{"blendedFrom":[subQ2,makeQuery(id+"F4.opExtrude","CAP_FACE",FACE,{"disambiguationData":[OSD([subQ0])],"isStart":false})],"blendedInto":[makeQuery(id+"F4.opExtrude","CAP_FACE",FACE,{"disambiguationData":[OSD([subQ0])],"isStart":false})]})])]})]}),makeQuery(id+"F43.opExtrude","SWEPT_FACE",FACE,{"disambiguationData":[OSD([sQuery(id+"F33.wireOp",EDGE,"E16.top")])]})]});}
            fillet(context, id + "F44", {"entities" : qUnion([Q0, Q1, Q2, Q3]), "radius" : 2.54 * mm, "tangentPropagation" : true, "allowEdgeOverflow" : false});
        }
    });
